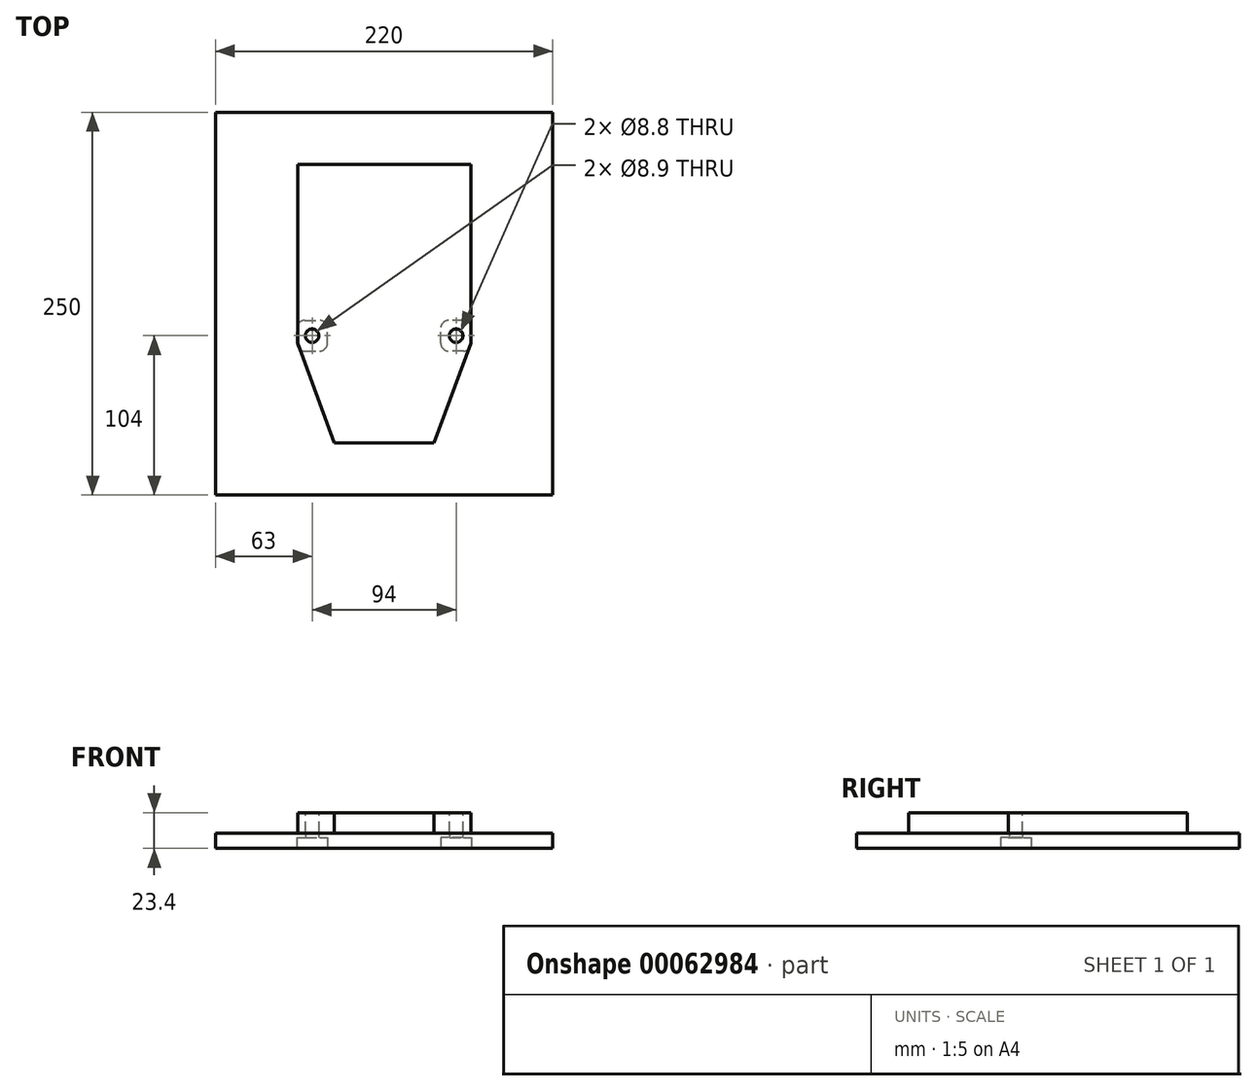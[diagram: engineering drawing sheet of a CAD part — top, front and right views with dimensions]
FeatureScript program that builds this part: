
annotation { "Feature Type Name" : "Feature", "Feature Type Description" : "" }
export const myFeature = defineFeature(function(context is Context, id is Id, definition is map)
    precondition{}
    {
        {
            var Q0;
            Q0=qCreatedBy(makeId("Top.planeOp"),FACE);
            var sketch = newSketch(context, id + "F0", { "sketchPlane" : qUnion([Q0])});
            skLineSegment(sketch, "E0", {"start": v(-56.5, 0) * mm, "end": v(-56.5, 117) * mm});
            skLineSegment(sketch, "E1", {"start": v(-56.5, 117) * mm, "end": v(56.5, 117) * mm});
            skLineSegment(sketch, "E2", {"start": v(56.5, 117) * mm, "end": v(56.5, 0) * mm});
            skLineSegment(sketch, "E3", {"start": v(56.5, 0) * mm, "end": v(32.5, -65) * mm});
            skLineSegment(sketch, "E4", {"start": v(32.5, -65) * mm, "end": v(-32.5, -65) * mm});
            skLineSegment(sketch, "E5", {"start": v(-32.5, -65) * mm, "end": v(-56.5, 0) * mm});
            skLineSegment(sketch, "E6", {"start": v(0, 0) * mm, "end": v(0, 117) * mm});
            skLineSegment(sketch, "E7", {"start": v(0, 0) * mm, "end": v(0, -65) * mm});
            skSolve(sketch);
        }
        {
            var Q0;
            Q0 = qSketchRegion(id + "F0", true);
            extrude(context, id + "F1", {"entities" : qUnion([Q0]), "depth" : 13.4 * mm});
        }
        {
            var Q0;
            Q0=makeQuery(id+"F1.opExtrude","CAP_FACE",FACE,{"disambiguationData":[OSD([sQuery(id+"F0.wireOp",EDGE,"E0"),sQuery(id+"F0.wireOp",EDGE,"E1"),sQuery(id+"F0.wireOp",EDGE,"E2"),sQuery(id+"F0.wireOp",EDGE,"E3"),sQuery(id+"F0.wireOp",EDGE,"E4"),sQuery(id+"F0.wireOp",EDGE,"E5")])],"isStart":false});
            var sketch = newSketch(context, id + "F2", { "sketchPlane" : qUnion([Q0])});
            skCircle(sketch, "E8", {"center": v(-47, 5) * mm, "radius": 4.45 * mm});
            skCircle(sketch, "E9", {"center": v(47, 5) * mm, "radius": 4.45 * mm});
            skSolve(sketch);
        }
        {
            var Q0;
            Q0 = qSketchRegion(id + "F2", true);
            extrude(context, id + "F3", {"entities" : qUnion([Q0]), "operationType" : NewBodyOperationType.REMOVE, "endBound" : BoundingType.THROUGH_ALL, "oppositeDirection" : true, "depth" : 25 * mm});
        }
        {
            var Q0;
            Q0=qCreatedBy(makeId("Top.planeOp"),FACE);
            var sketch = newSketch(context, id + "F4", { "sketchPlane" : qUnion([Q0])});
            skLineSegment(sketch, "E10.bottom", {"start": v(110, 151) * mm, "end": v(-110, 151) * mm});
            skLineSegment(sketch, "E10.top", {"start": v(110, -99) * mm, "end": v(-110, -99) * mm});
            skLineSegment(sketch, "E10.left", {"start": v(110, 151) * mm, "end": v(110, -99) * mm});
            skLineSegment(sketch, "E10.right", {"start": v(-110, 151) * mm, "end": v(-110, -99) * mm});
            skSolve(sketch);
        }
        {
            var Q0;
            Q0 = qSketchRegion(id + "F4", true);
            extrude(context, id + "F5", {"entities" : qUnion([Q0]), "oppositeDirection" : true, "depth" : 10 * mm});
        }
        {
            var Q0;
            Q0=makeQuery(id+"F5.opExtrude","CAP_FACE",FACE,{"disambiguationData":[OSD([sQuery(id+"F4.wireOp",EDGE,"E10.bottom"),sQuery(id+"F4.wireOp",EDGE,"E10.top"),sQuery(id+"F4.wireOp",EDGE,"E10.left"),sQuery(id+"F4.wireOp",EDGE,"E10.right")])],"isStart":false});
            var sketch = newSketch(context, id + "F6", { "sketchPlane" : qUnion([Q0])});
            skCircle(sketch, "E11", {"center": v(-47, -5) * mm, "radius": 4.4 * mm});
            skCircle(sketch, "E12", {"center": v(47, -5) * mm, "radius": 4.4 * mm});
            skSolve(sketch);
        }
        {
            var Q0;
            Q0 = qSketchRegion(id + "F6", true);
            var Q1;
            Q1=makeQuery(id+"F5.opExtrude","CAP_FACE",FACE,{"disambiguationData":[OSD([sQuery(id+"F4.wireOp",EDGE,"E10.bottom"),sQuery(id+"F4.wireOp",EDGE,"E10.top"),sQuery(id+"F4.wireOp",EDGE,"E10.left"),sQuery(id+"F4.wireOp",EDGE,"E10.right")])],"isStart":true});
            extrude(context, id + "F7", {"entities" : qUnion([Q0]), "operationType" : NewBodyOperationType.REMOVE, "endBound" : BoundingType.UP_TO_SURFACE, "oppositeDirection" : true, "endBoundEntityFace" : qUnion([Q1]), "depth" : 25 * mm});
        }
        {
            var Q0;
            Q0=makeQuery(id+"F5.opExtrude","CAP_FACE",FACE,{"disambiguationData":[OSD([sQuery(id+"F4.wireOp",EDGE,"E10.bottom"),sQuery(id+"F4.wireOp",EDGE,"E10.top"),sQuery(id+"F4.wireOp",EDGE,"E10.left"),sQuery(id+"F4.wireOp",EDGE,"E10.right")])],"isStart":false});
            var sketch = newSketch(context, id + "F9", { "sketchPlane" : qUnion([Q0])});
            skLineSegment(sketch, "E13.bottom", {"start": v(-57, 5) * mm, "end": v(-37, 5) * mm});
            skLineSegment(sketch, "E13.top", {"start": v(-57, -15) * mm, "end": v(-37, -15) * mm});
            skLineSegment(sketch, "E13.left", {"start": v(-57, 5) * mm, "end": v(-57, -15) * mm});
            skLineSegment(sketch, "E13.right", {"start": v(-37, 5) * mm, "end": v(-37, -15) * mm});
            skLineSegment(sketch, "E14", {"start": v(-47, -5) * mm, "end": v(-37, -5) * mm});
            skLineSegment(sketch, "E15", {"start": v(-47, -5) * mm, "end": v(-47, 5) * mm});
            skLineSegment(sketch, "E16.MirrorCS", {"start": v(57, 5) * mm, "end": v(37, 5) * mm});
            skLineSegment(sketch, "E17.MirrorCS", {"start": v(57, -15) * mm, "end": v(37, -15) * mm});
            skLineSegment(sketch, "E18.MirrorCS", {"start": v(57, 5) * mm, "end": v(57, -15) * mm});
            skLineSegment(sketch, "E19.MirrorCS", {"start": v(37, 5) * mm, "end": v(37, -15) * mm});
            skSolve(sketch);
        }
        {
            var Q0;
            Q0 = qSketchRegion(id + "F9", true);
            extrude(context, id + "F10", {"entities" : qUnion([Q0]), "operationType" : NewBodyOperationType.REMOVE, "oppositeDirection" : true, "depth" : 7 * mm});
        }
        {
            var Q0;
            Q0=makeQuery(id+"F10.boolean.opBoolean","COPY",EDGE,{"derivedFrom":makeQuery(id+"F10.opExtrude","SWEPT_EDGE",EDGE,{"disambiguationData":[OSD([sQuery(id+"F9.wireOp",EDGE,"E13.bottom"),sQuery(id+"F9.wireOp",EDGE,"E13.left")])]})});
            var Q1;
            Q1=makeQuery(id+"F10.boolean.opBoolean","COPY",EDGE,{"derivedFrom":makeQuery(id+"F10.opExtrude","SWEPT_EDGE",EDGE,{"disambiguationData":[OSD([sQuery(id+"F9.wireOp",EDGE,"E13.bottom"),sQuery(id+"F9.wireOp",EDGE,"E13.right")])]})});
            var Q2;
            Q2=makeQuery(id+"F10.boolean.opBoolean","COPY",EDGE,{"derivedFrom":makeQuery(id+"F10.opExtrude","SWEPT_EDGE",EDGE,{"disambiguationData":[OSD([sQuery(id+"F9.wireOp",EDGE,"E13.top"),sQuery(id+"F9.wireOp",EDGE,"E13.right")])]})});
            var Q3;
            Q3=makeQuery(id+"F10.boolean.opBoolean","COPY",EDGE,{"derivedFrom":makeQuery(id+"F10.opExtrude","SWEPT_EDGE",EDGE,{"disambiguationData":[OSD([sQuery(id+"F9.wireOp",EDGE,"E13.top"),sQuery(id+"F9.wireOp",EDGE,"E13.left")])]})});
            var Q4;
            Q4=makeQuery(id+"F10.boolean.opBoolean","COPY",EDGE,{"derivedFrom":makeQuery(id+"F10.opExtrude","SWEPT_EDGE",EDGE,{"disambiguationData":[OSD([sQuery(id+"F9.wireOp",EDGE,"E16.MirrorCS"),sQuery(id+"F9.wireOp",EDGE,"E18.MirrorCS")])]})});
            var Q5;
            Q5=makeQuery(id+"F10.boolean.opBoolean","COPY",EDGE,{"derivedFrom":makeQuery(id+"F10.opExtrude","SWEPT_EDGE",EDGE,{"disambiguationData":[OSD([sQuery(id+"F9.wireOp",EDGE,"E17.MirrorCS"),sQuery(id+"F9.wireOp",EDGE,"E18.MirrorCS")])]})});
            var Q6;
            Q6=makeQuery(id+"F10.boolean.opBoolean","COPY",EDGE,{"derivedFrom":makeQuery(id+"F10.opExtrude","SWEPT_EDGE",EDGE,{"disambiguationData":[OSD([sQuery(id+"F9.wireOp",EDGE,"E17.MirrorCS"),sQuery(id+"F9.wireOp",EDGE,"E19.MirrorCS")])]})});
            var Q7;
            Q7=makeQuery(id+"F10.boolean.opBoolean","COPY",EDGE,{"derivedFrom":makeQuery(id+"F10.opExtrude","SWEPT_EDGE",EDGE,{"disambiguationData":[OSD([sQuery(id+"F9.wireOp",EDGE,"E16.MirrorCS"),sQuery(id+"F9.wireOp",EDGE,"E19.MirrorCS")])]})});
            fillet(context, id + "F11", {"entities" : qUnion([Q0, Q1, Q2, Q3, Q4, Q5, Q6, Q7]), "radius" : 5 * mm, "tangentPropagation" : true, "allowEdgeOverflow" : false});
        }
    });
